# Revit family: Hinge_CI3850_ShutIt_SelfClosing-Set_DD-Technologies-Including-CI3000-Original-BadAss-Hinge
name_source: partatom
category: Specialty Equipment
units: mm (PartAtom-declared; Revit-internal decimal feet)

## family parameters
Always vertical = Yes
Cut with Voids When Loaded = No
Maintain Annotation Orientation = No
Part Type = Normal
Room Calculation Point = No
Round Connector Dimension = Use Diameter
Shared = No
Work Plane-Based = Yes

## types (1)
- CI3850 - Shut-It® Self-Closing BadAss™ Set Incl CI3000 BadAss Hinge
    Adjustable Total Length = 2.9-3.4” (74-97mm)
    Assembly Code = G2060.20 Fences and Gates
    Body Height = 3.2” (81mm)
    Body Width = 1.5” (38mm)
1.5” (38mm)
    Catalog Page = https://us.ddtech.com
    Color/Finish = Zinc Electroplated
    Default Elevation = 0 "
    Description = Self-closing hinge-closer set, includes one self-closing hinge plus one CI3000 Original BadAss™ hinge, weld-on, ADA suitable
    Gate Material = Steel / Ornamental Iron
    Hinge Material = Steel
    Horizontal Gap Adjustment (Variance) = 2-3⁄8” –  2-7⁄8” (61-74mm)
    Keynote = 32 31 00 Fence & Gates
    Load rating per gate*  (per pair of hinge) = 300 lb (140kg)
    Manufacturer = D&D Technologies
    Maximal Gate Weight*  (per pair of hinge) = 300 lb (140kg)
    Maximal Self-Closing Gate Weight*  (per pair of hinge) = 300 lb (140kg)
    Model = CI3850
    Product Name = Shut-It® Self-Closing BadAss™ Hinge Set
    Product Webpage with product image = https://us.ddtech.com
    Specification = https://us.ddtech.com
    Spring-Hinge Total Height = 5” (127mm)
    Type = Self-closing hinge set
    URL = https://ddtech.com
    Yoke Height = 4.1 (104mm)
    Yoke Thickness = 0.2” (5mm)
    Yoke Width = 1.5” (38mm)

## geometry (parser evidence)
native form markers: Sweep x17
no freeform markers — native parametric forms only
